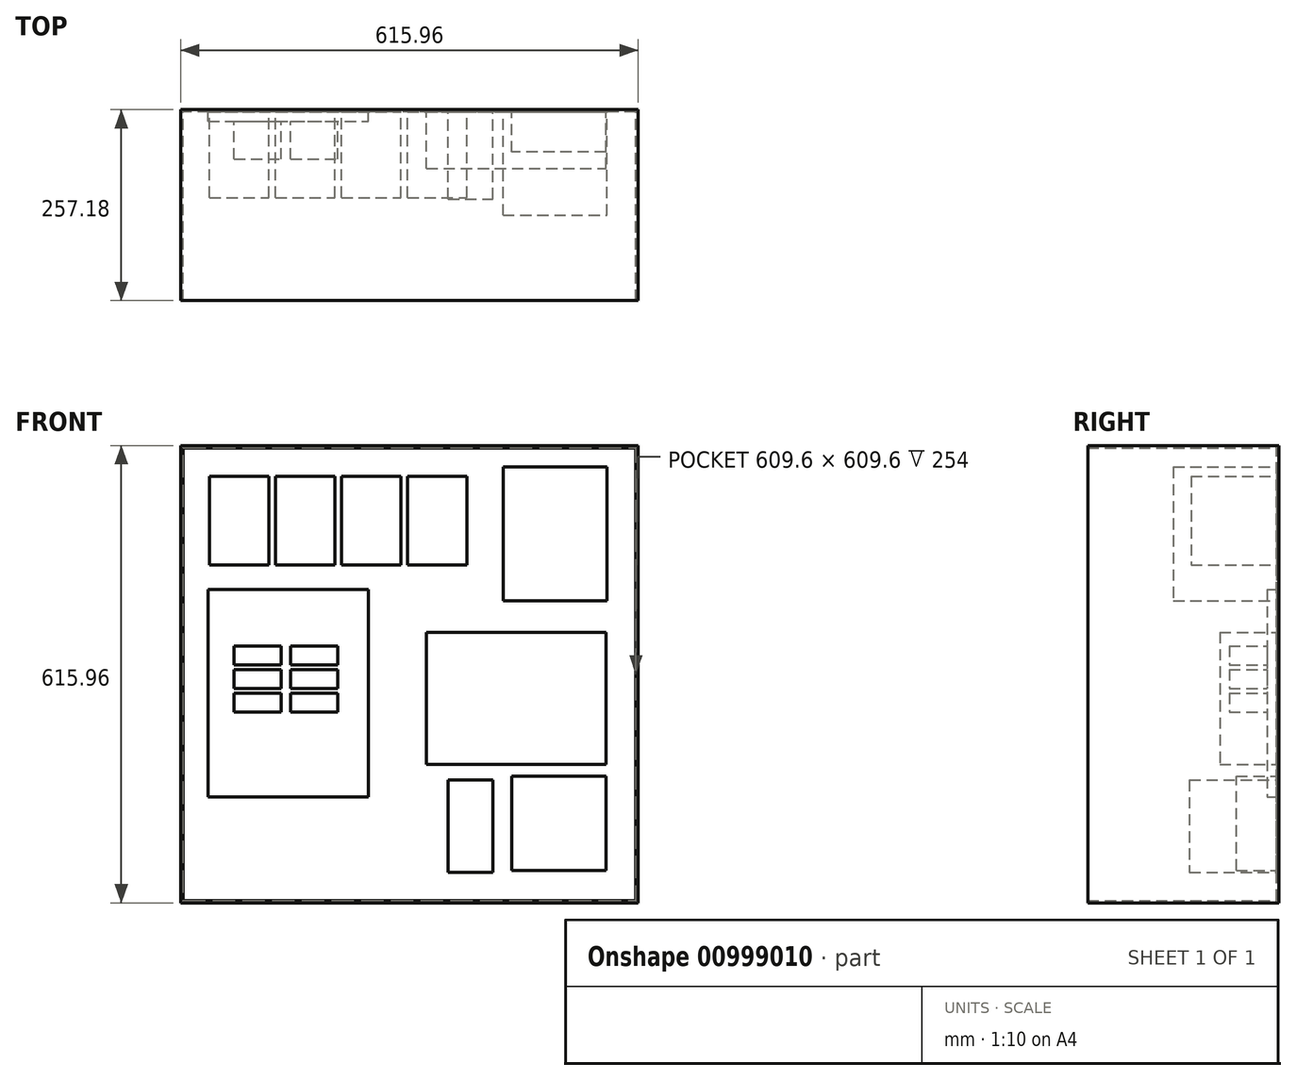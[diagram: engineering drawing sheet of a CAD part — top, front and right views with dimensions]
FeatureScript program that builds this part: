
annotation { "Feature Type Name" : "Feature", "Feature Type Description" : "" }
export const myFeature = defineFeature(function(context is Context, id is Id, definition is map)
    precondition{}
    {
        {
            var Q0;
            Q0=qCreatedBy(makeId("Front.planeOp"),FACE);
            var sketch = newSketch(context, id + "F0", { "sketchPlane" : qUnion([Q0])});
            skLineSegment(sketch, "E0.bottom", {"start": v(-304.8, 304.8) * mm, "end": v(304.8, 304.8) * mm});
            skLineSegment(sketch, "E0.top", {"start": v(-304.8, -304.8) * mm, "end": v(304.8, -304.8) * mm});
            skLineSegment(sketch, "E0.left", {"start": v(-304.8, 304.8) * mm, "end": v(-304.8, -304.8) * mm});
            skLineSegment(sketch, "E0.right", {"start": v(304.8, 304.8) * mm, "end": v(304.8, -304.8) * mm});
            skLineSegment(sketch, "E1.bottom", {"start": v(-307.98, 307.97) * mm, "end": v(307.97, 307.97) * mm});
            skLineSegment(sketch, "E1.top", {"start": v(-307.98, -307.98) * mm, "end": v(307.97, -307.98) * mm});
            skLineSegment(sketch, "E1.left", {"start": v(-307.98, 307.97) * mm, "end": v(-307.98, -307.98) * mm});
            skLineSegment(sketch, "E1.right", {"start": v(307.97, 307.97) * mm, "end": v(307.97, -307.98) * mm});
            skSolve(sketch);
        }
        {
            var Q0;
            Q0=makeQuery(id+"F0.imprint","IMPRINT",FACE,{"disambiguationData":[TD([[makeQuery(id+"F0.imprint","IMPRINT",EDGE,{"derivedFrom":sQuery(id+"F0.wireOp",EDGE,"E0.bottom")}),1.0]])]});
            extrude(context, id + "F1", {"entities" : qUnion([Q0]), "depth" : 257.18 * mm, "offsetDistance" : 30.48 * mm});
        }
        {
            var Q0;
            Q0=makeQuery(id+"F1.opExtrude","SWEPT_FACE",FACE,{"disambiguationData":[OSD([sQuery(id+"F0.wireOp",EDGE,"E0.bottom")])]});
            var sketch = newSketch(context, id + "F2", { "sketchPlane" : qUnion([Q0])});
            skLineSegment(sketch, "E2", {"start": v(-304.8, 3.17) * mm, "end": v(304.8, 3.18) * mm});
            skSolve(sketch);
        }
        {
            var Q0;
            {var subQ0=sQuery(id+"F2.wireOp",EDGE,"E2");Q0=makeQuery(id+"F2.imprint","IMPRINT",FACE,{"disambiguationData":[TD([[makeQuery(id+"F2.imprint","IMPRINT",EDGE,{"derivedFrom":subQ0}),-1.0]])]});}
            extrude(context, id + "F3", {"entities" : qUnion([Q0]), "operationType" : NewBodyOperationType.ADD, "endBound" : BoundingType.UP_TO_NEXT, "depth" : 30.48 * mm, "offsetDistance" : 30.48 * mm});
        }
        {
            var Q0;
            Q0=makeQuery(id+"F3.opExtrude","SWEPT_FACE",FACE,{"disambiguationData":[OSD([sQuery(id+"F2.wireOp",EDGE,"E2")])]});
            var sketch = newSketch(context, id + "F4", { "sketchPlane" : qUnion([Q0])});
            skLineSegment(sketch, "E3.bottom", {"start": v(-269.3, 266.65) * mm, "end": v(-189.3, 266.65) * mm});
            skLineSegment(sketch, "E3.top", {"start": v(-269.3, 146.76) * mm, "end": v(-189.3, 146.76) * mm});
            skLineSegment(sketch, "E3.left", {"start": v(-269.3, 266.65) * mm, "end": v(-269.3, 146.76) * mm});
            skLineSegment(sketch, "E3.right", {"start": v(-189.3, 266.65) * mm, "end": v(-189.3, 146.76) * mm});
            skSolve(sketch);
        }
        {
            var Q0;
            Q0=makeQuery(id+"F4.imprint","IMPRINT",FACE,{"disambiguationData":[TD([[makeQuery(id+"F4.imprint","IMPRINT",EDGE,{"derivedFrom":sQuery(id+"F4.wireOp",EDGE,"E3.bottom")}),-1.0]])]});
            extrude(context, id + "F5", {"entities" : qUnion([Q0]), "depth" : 115.06 * mm, "offsetDistance" : 25.4 * mm});
        }
        {
            var Q0;
            Q0=makeQuery(id+"F5.opExtrude","SWEPT_BODY",BODY,{"disambiguationData":[OSD([sQuery(id+"F4.wireOp",EDGE,"E3.bottom"),sQuery(id+"F4.wireOp",EDGE,"E3.top"),sQuery(id+"F4.wireOp",EDGE,"E3.left"),sQuery(id+"F4.wireOp",EDGE,"E3.right")])]});
            transform(context, id + "F6", {"entities" : qUnion([Q0]), "transformType" : TransformType.TRANSLATION_3D, "dx" : 88.9 * mm, "dy" : 0 * mm, "dz" : 0 * mm, "makeCopy" : true});
        }
        {
            var Q0;
            Q0=makeQuery(id+"F6.opPattern","COPY",BODY,{"derivedFrom":makeQuery(id+"F5.opExtrude","SWEPT_BODY",BODY,{"disambiguationData":[OSD([sQuery(id+"F4.wireOp",EDGE,"E3.bottom"),sQuery(id+"F4.wireOp",EDGE,"E3.top"),sQuery(id+"F4.wireOp",EDGE,"E3.left"),sQuery(id+"F4.wireOp",EDGE,"E3.right")])]}),"instanceName":"1"});
            transform(context, id + "F7", {"entities" : qUnion([Q0]), "transformType" : TransformType.TRANSLATION_3D, "dx" : 88.9 * mm, "dy" : 0 * mm, "dz" : 0 * mm, "makeCopy" : true});
        }
        {
            var Q0;
            Q0=makeQuery(id+"F7.opPattern","COPY",BODY,{"derivedFrom":makeQuery(id+"F6.opPattern","COPY",BODY,{"derivedFrom":makeQuery(id+"F5.opExtrude","SWEPT_BODY",BODY,{"disambiguationData":[OSD([sQuery(id+"F4.wireOp",EDGE,"E3.bottom"),sQuery(id+"F4.wireOp",EDGE,"E3.top"),sQuery(id+"F4.wireOp",EDGE,"E3.left"),sQuery(id+"F4.wireOp",EDGE,"E3.right")])]}),"instanceName":"1"}),"instanceName":"1"});
            transform(context, id + "F8", {"entities" : qUnion([Q0]), "transformType" : TransformType.TRANSLATION_3D, "dx" : 88.9 * mm, "dy" : 0 * mm, "dz" : 0 * mm, "makeCopy" : true});
        }
        {
            var Q0;
            Q0=makeQuery(id+"F3.opExtrude","SWEPT_FACE",FACE,{"disambiguationData":[OSD([sQuery(id+"F2.wireOp",EDGE,"E2")])]});
            var sketch = newSketch(context, id + "F9", { "sketchPlane" : qUnion([Q0])});
            skLineSegment(sketch, "E4.bottom", {"start": v(126.23, 278.84) * mm, "end": v(266.18, 278.84) * mm});
            skLineSegment(sketch, "E4.top", {"start": v(126.23, 98.75) * mm, "end": v(266.18, 98.75) * mm});
            skLineSegment(sketch, "E4.left", {"start": v(126.23, 278.84) * mm, "end": v(126.23, 98.75) * mm});
            skLineSegment(sketch, "E4.right", {"start": v(266.18, 278.84) * mm, "end": v(266.18, 98.75) * mm});
            skSolve(sketch);
        }
        {
            var Q0;
            Q0=makeQuery(id+"F9.imprint","IMPRINT",FACE,{"disambiguationData":[TD([[makeQuery(id+"F9.imprint","IMPRINT",EDGE,{"derivedFrom":sQuery(id+"F9.wireOp",EDGE,"E4.bottom")}),-1.0]])]});
            extrude(context, id + "F10", {"entities" : qUnion([Q0]), "depth" : 138.94 * mm, "offsetDistance" : 25.4 * mm});
        }
        {
            var Q0;
            Q0=makeQuery(id+"F3.opExtrude","SWEPT_FACE",FACE,{"disambiguationData":[OSD([sQuery(id+"F2.wireOp",EDGE,"E2")])]});
            var sketch = newSketch(context, id + "F11", { "sketchPlane" : qUnion([Q0])});
            skLineSegment(sketch, "E5.bottom", {"start": v(-271.09, 114.3) * mm, "end": v(-55.19, 114.3) * mm});
            skLineSegment(sketch, "E5.top", {"start": v(-271.09, -165.1) * mm, "end": v(-55.19, -165.1) * mm});
            skLineSegment(sketch, "E5.left", {"start": v(-271.09, 114.3) * mm, "end": v(-271.09, -165.1) * mm});
            skLineSegment(sketch, "E5.right", {"start": v(-55.19, 114.3) * mm, "end": v(-55.19, -165.1) * mm});
            skSolve(sketch);
        }
        {
            var Q0;
            Q0=makeQuery(id+"F11.imprint","IMPRINT",FACE,{"disambiguationData":[TD([[makeQuery(id+"F11.imprint","IMPRINT",EDGE,{"derivedFrom":sQuery(id+"F11.wireOp",EDGE,"E5.bottom")}),-1.0]])]});
            extrude(context, id + "F12", {"entities" : qUnion([Q0]), "depth" : 12.7 * mm, "offsetDistance" : 25.4 * mm});
        }
        {
            var Q0;
            Q0=makeQuery(id+"F12.opExtrude","CAP_FACE",FACE,{"disambiguationData":[OSD([sQuery(id+"F11.wireOp",EDGE,"E5.bottom"),sQuery(id+"F11.wireOp",EDGE,"E5.top"),sQuery(id+"F11.wireOp",EDGE,"E5.left"),sQuery(id+"F11.wireOp",EDGE,"E5.right")])],"isStart":false});
            var sketch = newSketch(context, id + "F13", { "sketchPlane" : qUnion([Q0])});
            skLineSegment(sketch, "E6.bottom", {"start": v(-236.16, 38.1) * mm, "end": v(-172.66, 38.1) * mm});
            skLineSegment(sketch, "E6.top", {"start": v(-236.16, 12.7) * mm, "end": v(-172.66, 12.7) * mm});
            skLineSegment(sketch, "E6.left", {"start": v(-236.16, 38.1) * mm, "end": v(-236.16, 12.7) * mm});
            skLineSegment(sketch, "E6.right", {"start": v(-172.66, 38.1) * mm, "end": v(-172.66, 12.7) * mm});
            skSolve(sketch);
        }
        {
            var Q0;
            Q0=makeQuery(id+"F13.imprint","IMPRINT",FACE,{"disambiguationData":[TD([[makeQuery(id+"F13.imprint","IMPRINT",EDGE,{"derivedFrom":sQuery(id+"F13.wireOp",EDGE,"E6.bottom")}),-1.0]])]});
            extrude(context, id + "F14", {"entities" : qUnion([Q0]), "depth" : 50.8 * mm, "offsetDistance" : 25.4 * mm});
        }
        {
            var Q0;
            Q0=makeQuery(id+"F14.opExtrude","SWEPT_BODY",BODY,{"disambiguationData":[OSD([sQuery(id+"F13.wireOp",EDGE,"E6.bottom"),sQuery(id+"F13.wireOp",EDGE,"E6.top"),sQuery(id+"F13.wireOp",EDGE,"E6.left"),sQuery(id+"F13.wireOp",EDGE,"E6.right")])]});
            transform(context, id + "F15", {"entities" : qUnion([Q0]), "transformType" : TransformType.TRANSLATION_3D, "dx" : 0 * mm, "dy" : 0 * mm, "dz" : -31.75 * mm, "makeCopy" : true});
        }
        {
            var Q0;
            Q0=makeQuery(id+"F14.opExtrude","SWEPT_BODY",BODY,{"disambiguationData":[OSD([sQuery(id+"F13.wireOp",EDGE,"E6.bottom"),sQuery(id+"F13.wireOp",EDGE,"E6.top"),sQuery(id+"F13.wireOp",EDGE,"E6.left"),sQuery(id+"F13.wireOp",EDGE,"E6.right")])]});
            transform(context, id + "F16", {"entities" : qUnion([Q0]), "transformType" : TransformType.TRANSLATION_3D, "dx" : 76.2 * mm, "dy" : 0 * mm, "dz" : 0 * mm, "makeCopy" : true});
        }
        {
            var Q0;
            Q0=makeQuery(id+"F15.opPattern","COPY",BODY,{"derivedFrom":makeQuery(id+"F14.opExtrude","SWEPT_BODY",BODY,{"disambiguationData":[OSD([sQuery(id+"F13.wireOp",EDGE,"E6.bottom"),sQuery(id+"F13.wireOp",EDGE,"E6.top"),sQuery(id+"F13.wireOp",EDGE,"E6.left"),sQuery(id+"F13.wireOp",EDGE,"E6.right")])]}),"instanceName":"1"});
            transform(context, id + "F17", {"entities" : qUnion([Q0]), "transformType" : TransformType.TRANSLATION_3D, "dx" : 76.2 * mm, "dy" : 0 * mm, "dz" : 0 * mm, "makeCopy" : true});
        }
        {
            var Q0;
            Q0=makeQuery(id+"F15.opPattern","COPY",BODY,{"derivedFrom":makeQuery(id+"F14.opExtrude","SWEPT_BODY",BODY,{"disambiguationData":[OSD([sQuery(id+"F13.wireOp",EDGE,"E6.bottom"),sQuery(id+"F13.wireOp",EDGE,"E6.top"),sQuery(id+"F13.wireOp",EDGE,"E6.left"),sQuery(id+"F13.wireOp",EDGE,"E6.right")])]}),"instanceName":"1"});
            transform(context, id + "F18", {"entities" : qUnion([Q0]), "transformType" : TransformType.TRANSLATION_3D, "dx" : 0 * mm, "dy" : 0 * mm, "dz" : -31.75 * mm, "makeCopy" : true});
        }
        {
            var Q0;
            Q0=makeQuery(id+"F18.opPattern","COPY",BODY,{"derivedFrom":makeQuery(id+"F15.opPattern","COPY",BODY,{"derivedFrom":makeQuery(id+"F14.opExtrude","SWEPT_BODY",BODY,{"disambiguationData":[OSD([sQuery(id+"F13.wireOp",EDGE,"E6.bottom"),sQuery(id+"F13.wireOp",EDGE,"E6.top"),sQuery(id+"F13.wireOp",EDGE,"E6.left"),sQuery(id+"F13.wireOp",EDGE,"E6.right")])]}),"instanceName":"1"}),"instanceName":"1"});
            transform(context, id + "F19", {"entities" : qUnion([Q0]), "transformType" : TransformType.TRANSLATION_3D, "dx" : 76.2 * mm, "dy" : 0 * mm, "dz" : 0 * mm, "makeCopy" : true});
        }
        {
            var Q0;
            Q0=makeQuery(id+"F3.opExtrude","SWEPT_FACE",FACE,{"disambiguationData":[OSD([sQuery(id+"F2.wireOp",EDGE,"E2")])]});
            var sketch = newSketch(context, id + "F20", { "sketchPlane" : qUnion([Q0])});
            skLineSegment(sketch, "E7.bottom", {"start": v(264.4, -264.45) * mm, "end": v(137.4, -264.45) * mm});
            skLineSegment(sketch, "E7.top", {"start": v(264.4, -137.45) * mm, "end": v(137.4, -137.45) * mm});
            skLineSegment(sketch, "E7.left", {"start": v(264.4, -264.45) * mm, "end": v(264.4, -137.45) * mm});
            skLineSegment(sketch, "E7.right", {"start": v(137.4, -264.45) * mm, "end": v(137.4, -137.45) * mm});
            skSolve(sketch);
        }
        {
            var Q0;
            Q0=makeQuery(id+"F20.imprint","IMPRINT",FACE,{"disambiguationData":[TD([[makeQuery(id+"F20.imprint","IMPRINT",EDGE,{"derivedFrom":sQuery(id+"F20.wireOp",EDGE,"E7.bottom")}),-1.0]])]});
            extrude(context, id + "F21", {"entities" : qUnion([Q0]), "depth" : 53.97 * mm, "offsetDistance" : 25.4 * mm});
        }
        {
            var Q0;
            Q0=makeQuery(id+"F3.opExtrude","SWEPT_FACE",FACE,{"disambiguationData":[OSD([sQuery(id+"F2.wireOp",EDGE,"E2")])]});
            var sketch = newSketch(context, id + "F22", { "sketchPlane" : qUnion([Q0])});
            skLineSegment(sketch, "E8.bottom", {"start": v(23.13, 56.56) * mm, "end": v(264.43, 56.56) * mm});
            skLineSegment(sketch, "E8.top", {"start": v(23.13, -121.24) * mm, "end": v(264.43, -121.24) * mm});
            skLineSegment(sketch, "E8.left", {"start": v(23.13, 56.56) * mm, "end": v(23.13, -121.24) * mm});
            skLineSegment(sketch, "E8.right", {"start": v(264.43, 56.56) * mm, "end": v(264.43, -121.24) * mm});
            skSolve(sketch);
        }
        {
            var Q0;
            Q0=makeQuery(id+"F22.imprint","IMPRINT",FACE,{"disambiguationData":[TD([[makeQuery(id+"F22.imprint","IMPRINT",EDGE,{"derivedFrom":sQuery(id+"F22.wireOp",EDGE,"E8.bottom")}),-1.0]])]});
            extrude(context, id + "F23", {"entities" : qUnion([Q0]), "depth" : 76.2 * mm, "offsetDistance" : 25.4 * mm});
        }
        {
            var Q0;
            Q0=makeQuery(id+"F3.opExtrude","SWEPT_FACE",FACE,{"disambiguationData":[OSD([sQuery(id+"F2.wireOp",EDGE,"E2")])]});
            var sketch = newSketch(context, id + "F24", { "sketchPlane" : qUnion([Q0])});
            skLineSegment(sketch, "E9.bottom", {"start": v(52.05, -142.75) * mm, "end": v(112, -142.75) * mm});
            skLineSegment(sketch, "E9.top", {"start": v(52.05, -266.7) * mm, "end": v(112, -266.7) * mm});
            skLineSegment(sketch, "E9.left", {"start": v(52.05, -142.75) * mm, "end": v(52.05, -266.7) * mm});
            skLineSegment(sketch, "E9.right", {"start": v(112, -142.75) * mm, "end": v(112, -266.7) * mm});
            skSolve(sketch);
        }
        {
            var Q0;
            Q0=makeQuery(id+"F24.imprint","IMPRINT",FACE,{"disambiguationData":[TD([[makeQuery(id+"F24.imprint","IMPRINT",EDGE,{"derivedFrom":sQuery(id+"F24.wireOp",EDGE,"E9.bottom")}),-1.0]])]});
            extrude(context, id + "F25", {"entities" : qUnion([Q0]), "depth" : 117.1 * mm, "offsetDistance" : 25.4 * mm});
        }
    });
